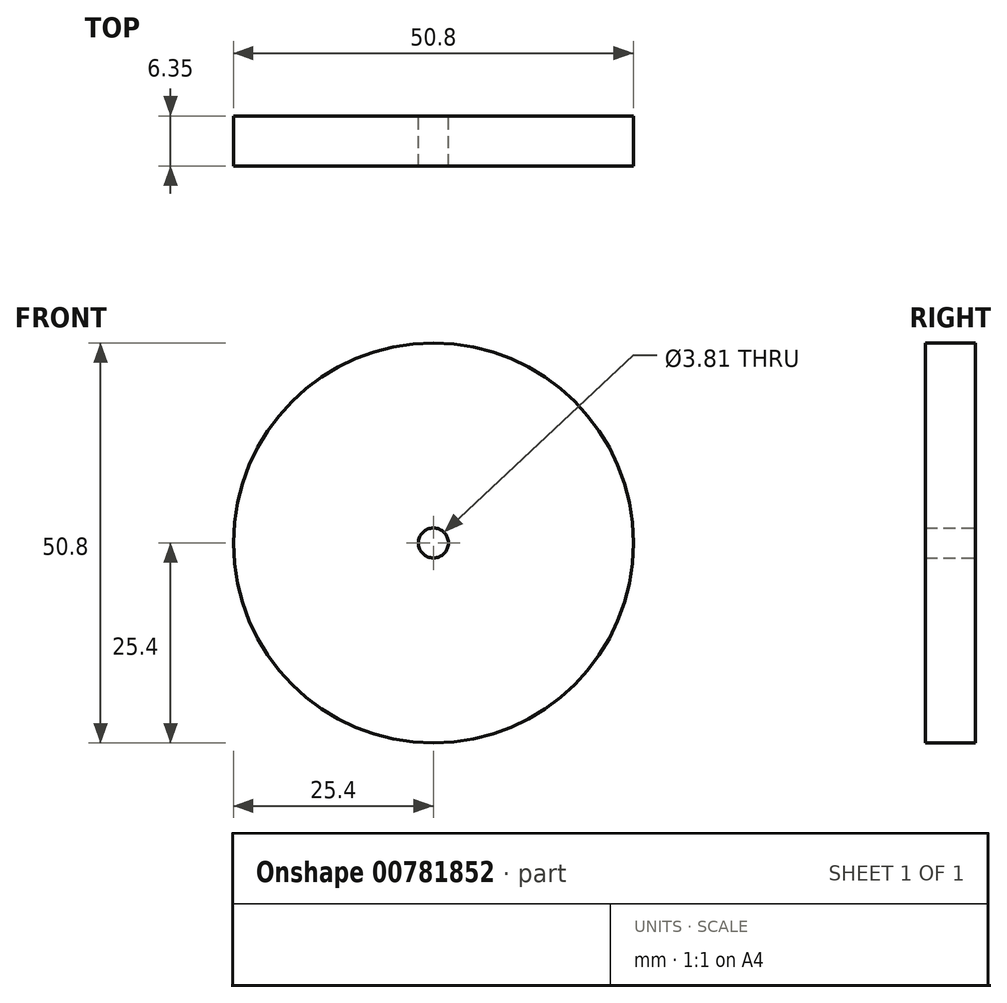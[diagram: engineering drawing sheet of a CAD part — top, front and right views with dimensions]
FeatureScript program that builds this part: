
annotation { "Feature Type Name" : "Feature", "Feature Type Description" : "" }
export const myFeature = defineFeature(function(context is Context, id is Id, definition is map)
    precondition{}
    {
        {
            var Q0;
            Q0=qCreatedBy(makeId("Front.planeOp"),FACE);
            var sketch = newSketch(context, id + "F0", { "sketchPlane" : qUnion([Q0])});
            skCircle(sketch, "E0", {"center": v(0, 0) * mm, "radius": 25.4 * mm});
            skCircle(sketch, "E1", {"center": v(0, 0) * mm, "radius": 1.9 * mm});
            skSolve(sketch);
        }
        {
            var Q0;
            Q0=makeQuery(id+"F0.imprint","IMPRINT",FACE,{"disambiguationData":[TD([[makeQuery(id+"F0.imprint","IMPRINT",EDGE,{"derivedFrom":sQuery(id+"F0.wireOp",EDGE,"E0")}),1.0]])]});
            extrude(context, id + "F1", {"entities" : qUnion([Q0]), "depth" : 6.35 * mm, "offsetDistance" : 25.4 * mm});
        }
    });
